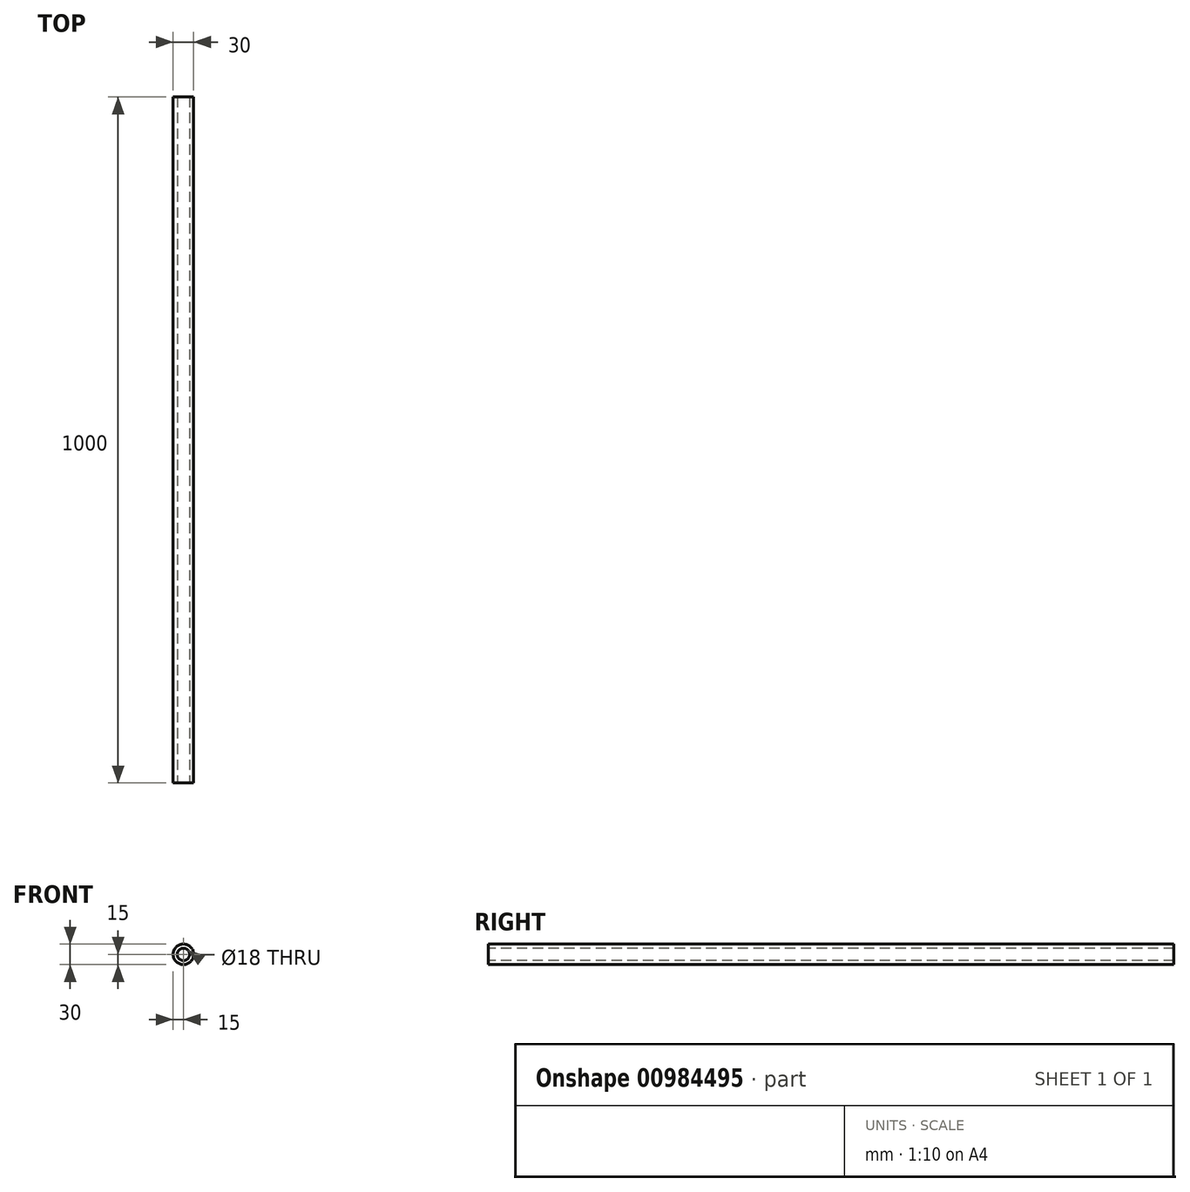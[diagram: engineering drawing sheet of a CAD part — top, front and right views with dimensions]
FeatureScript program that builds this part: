
annotation { "Feature Type Name" : "Feature", "Feature Type Description" : "" }
export const myFeature = defineFeature(function(context is Context, id is Id, definition is map)
    precondition{}
    {
        {
            var Q0;
            Q0=qCreatedBy(makeId("Front.planeOp"),FACE);
            var sketch = newSketch(context, id + "F0", { "sketchPlane" : qUnion([Q0])});
            skCircle(sketch, "E0", {"center": v(0, 0) * mm, "radius": 9 * mm});
            skCircle(sketch, "E1", {"center": v(0, 0) * mm, "radius": 15 * mm});
            skSolve(sketch);
        }
        {
            var Q0;
            Q0=makeQuery(id+"F0.imprint","IMPRINT",FACE,{"disambiguationData":[TD([[makeQuery(id+"F0.imprint","IMPRINT",EDGE,{"derivedFrom":sQuery(id+"F0.wireOp",EDGE,"E0")}),-1.0]])]});
            extrude(context, id + "F1", {"entities" : qUnion([Q0]), "oppositeDirection" : true, "depth" : 1000 * mm, "offsetDistance" : 25 * mm});
        }
    });
